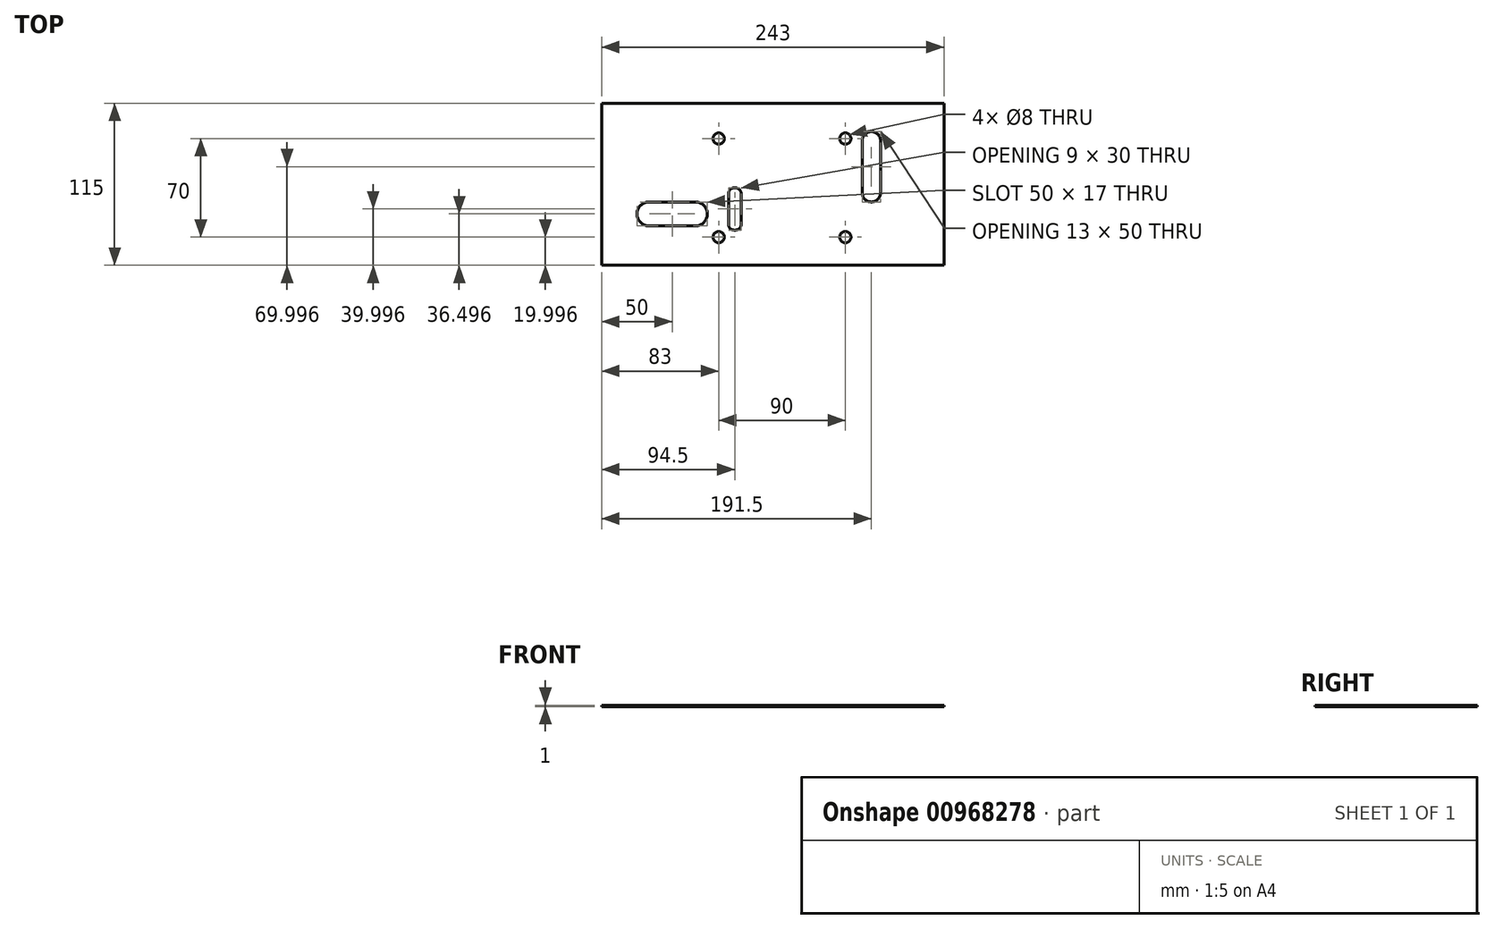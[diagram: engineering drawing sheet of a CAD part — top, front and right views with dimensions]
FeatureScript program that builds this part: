
annotation { "Feature Type Name" : "Feature", "Feature Type Description" : "" }
export const myFeature = defineFeature(function(context is Context, id is Id, definition is map)
    precondition{}
    {
        {
            var Q0;
            Q0=qCreatedBy(makeId("Top.planeOp"),FACE);
            var sketch = newSketch(context, id + "F0", { "sketchPlane" : qUnion([Q0])});
            skLineSegment(sketch, "E0.bottom", {"start": v(-185, 200.86) * mm, "end": v(58, 200.86) * mm});
            skLineSegment(sketch, "E0.top", {"start": v(-185, 0.86) * mm, "end": v(58, 0.86) * mm});
            skLineSegment(sketch, "E0.left", {"start": v(-185, 200.86) * mm, "end": v(-185, 0.86) * mm});
            skLineSegment(sketch, "E0.right", {"start": v(58, 200.86) * mm, "end": v(58, 0.86) * mm});
            skLineSegment(sketch, "E1", {"start": v(-185, 115.86) * mm, "end": v(58, 115.86) * mm});
            skLineSegment(sketch, "E2.bottom", {"start": v(6.6, 95.86) * mm, "end": v(6.4, 95.86) * mm});
            skLineSegment(sketch, "E2.top", {"start": v(6.6, 45.86) * mm, "end": v(6.4, 45.86) * mm});
            skLineSegment(sketch, "E2.left", {"start": v(13, 89.46) * mm, "end": v(13, 52.26) * mm});
            skLineSegment(sketch, "E2.right", {"start": v(0, 89.46) * mm, "end": v(0, 52.26) * mm});
            skLineSegment(sketch, "E3.bottom", {"start": v(-91, 55.86) * mm, "end": v(-90, 55.86) * mm});
            skLineSegment(sketch, "E3.top", {"start": v(-91, 25.86) * mm, "end": v(-90, 25.86) * mm});
            skLineSegment(sketch, "E3.left", {"start": v(-95, 51.86) * mm, "end": v(-95, 29.86) * mm});
            skLineSegment(sketch, "E3.right", {"start": v(-86, 51.86) * mm, "end": v(-86, 29.86) * mm});
            skLineSegment(sketch, "E4.bottom", {"start": v(-151.5, 45.86) * mm, "end": v(-118.5, 45.86) * mm});
            skLineSegment(sketch, "E4.top", {"start": v(-151.5, 28.86) * mm, "end": v(-118.5, 28.86) * mm});
            skLineSegment(sketch, "E4.left", {"start": v(-160, 37.36) * mm, "end": v(-160, 37.36) * mm});
            skLineSegment(sketch, "E4.right", {"start": v(-110, 37.36) * mm, "end": v(-110, 37.36) * mm});
            skCircle(sketch, "E5", {"center": v(-12, 20.86) * mm, "radius": 4 * mm});
            skCircle(sketch, "E6", {"center": v(-12, 90.86) * mm, "radius": 4 * mm});
            skCircle(sketch, "E7", {"center": v(-102, 90.86) * mm, "radius": 4 * mm});
            skCircle(sketch, "E8", {"center": v(-102, 20.86) * mm, "radius": 4 * mm});
            skPoint(sketch, "E9.visualSharp", {"position": v(0, 95.86) * mm});
            skArc(sketch, "E9.filletArc", {"start": v(6.4, 95.86) * mm, "mid": v(1.87, 93.98) * mm, "end": v(0, 89.46) * mm});
            skPoint(sketch, "E10.visualSharp", {"position": v(13, 95.86) * mm});
            skArc(sketch, "E10.filletArc", {"start": v(13, 89.46) * mm, "mid": v(11.13, 93.98) * mm, "end": v(6.6, 95.86) * mm});
            skPoint(sketch, "E11.visualSharp", {"position": v(13, 45.86) * mm});
            skArc(sketch, "E11.filletArc", {"start": v(6.6, 45.86) * mm, "mid": v(11.13, 47.73) * mm, "end": v(13, 52.26) * mm});
            skPoint(sketch, "E12.visualSharp", {"position": v(0, 45.86) * mm});
            skArc(sketch, "E12.filletArc", {"start": v(0, 52.26) * mm, "mid": v(1.87, 47.73) * mm, "end": v(6.4, 45.86) * mm});
            skPoint(sketch, "E13.visualSharp", {"position": v(-110, 45.86) * mm});
            skArc(sketch, "E13.filletArc", {"start": v(-110, 37.36) * mm, "mid": v(-112.49, 43.37) * mm, "end": v(-118.5, 45.86) * mm});
            skPoint(sketch, "E14.visualSharp", {"position": v(-110, 28.86) * mm});
            skArc(sketch, "E14.filletArc", {"start": v(-118.5, 28.86) * mm, "mid": v(-112.49, 31.35) * mm, "end": v(-110, 37.36) * mm});
            skPoint(sketch, "E15.visualSharp", {"position": v(-160, 45.86) * mm});
            skArc(sketch, "E15.filletArc", {"start": v(-151.5, 45.86) * mm, "mid": v(-157.51, 43.37) * mm, "end": v(-160, 37.36) * mm});
            skPoint(sketch, "E16.visualSharp", {"position": v(-160, 28.86) * mm});
            skArc(sketch, "E16.filletArc", {"start": v(-160, 37.36) * mm, "mid": v(-157.51, 31.35) * mm, "end": v(-151.5, 28.86) * mm});
            skPoint(sketch, "E17.visualSharp", {"position": v(-95, 55.86) * mm});
            skArc(sketch, "E17.filletArc", {"start": v(-91, 55.86) * mm, "mid": v(-93.83, 54.68) * mm, "end": v(-95, 51.86) * mm});
            skPoint(sketch, "E18.visualSharp", {"position": v(-86, 55.86) * mm});
            skArc(sketch, "E18.filletArc", {"start": v(-86, 51.86) * mm, "mid": v(-87.17, 54.68) * mm, "end": v(-90, 55.86) * mm});
            skPoint(sketch, "E19.visualSharp", {"position": v(-86, 25.86) * mm});
            skArc(sketch, "E19.filletArc", {"start": v(-90, 25.86) * mm, "mid": v(-87.17, 27.03) * mm, "end": v(-86, 29.86) * mm});
            skPoint(sketch, "E20.visualSharp", {"position": v(-95, 25.86) * mm});
            skArc(sketch, "E20.filletArc", {"start": v(-95, 29.86) * mm, "mid": v(-93.83, 27.03) * mm, "end": v(-91, 25.86) * mm});
            skSolve(sketch);
        }
        {
            var Q0;
            {var subQ1=sQuery(id+"F0.wireOp",EDGE,"E0.top");Q0=makeQuery(id+"F0.imprint","IMPRINT",FACE,{"disambiguationData":[TD([[makeQuery(id+"F0.imprint","IMPRINT",EDGE,{"derivedFrom":subQ1}),1.0]])]});}
            extrude(context, id + "F1", {"entities" : qUnion([Q0]), "depth" : 1 * mm, "offsetDistance" : 25 * mm});
        }
    });
